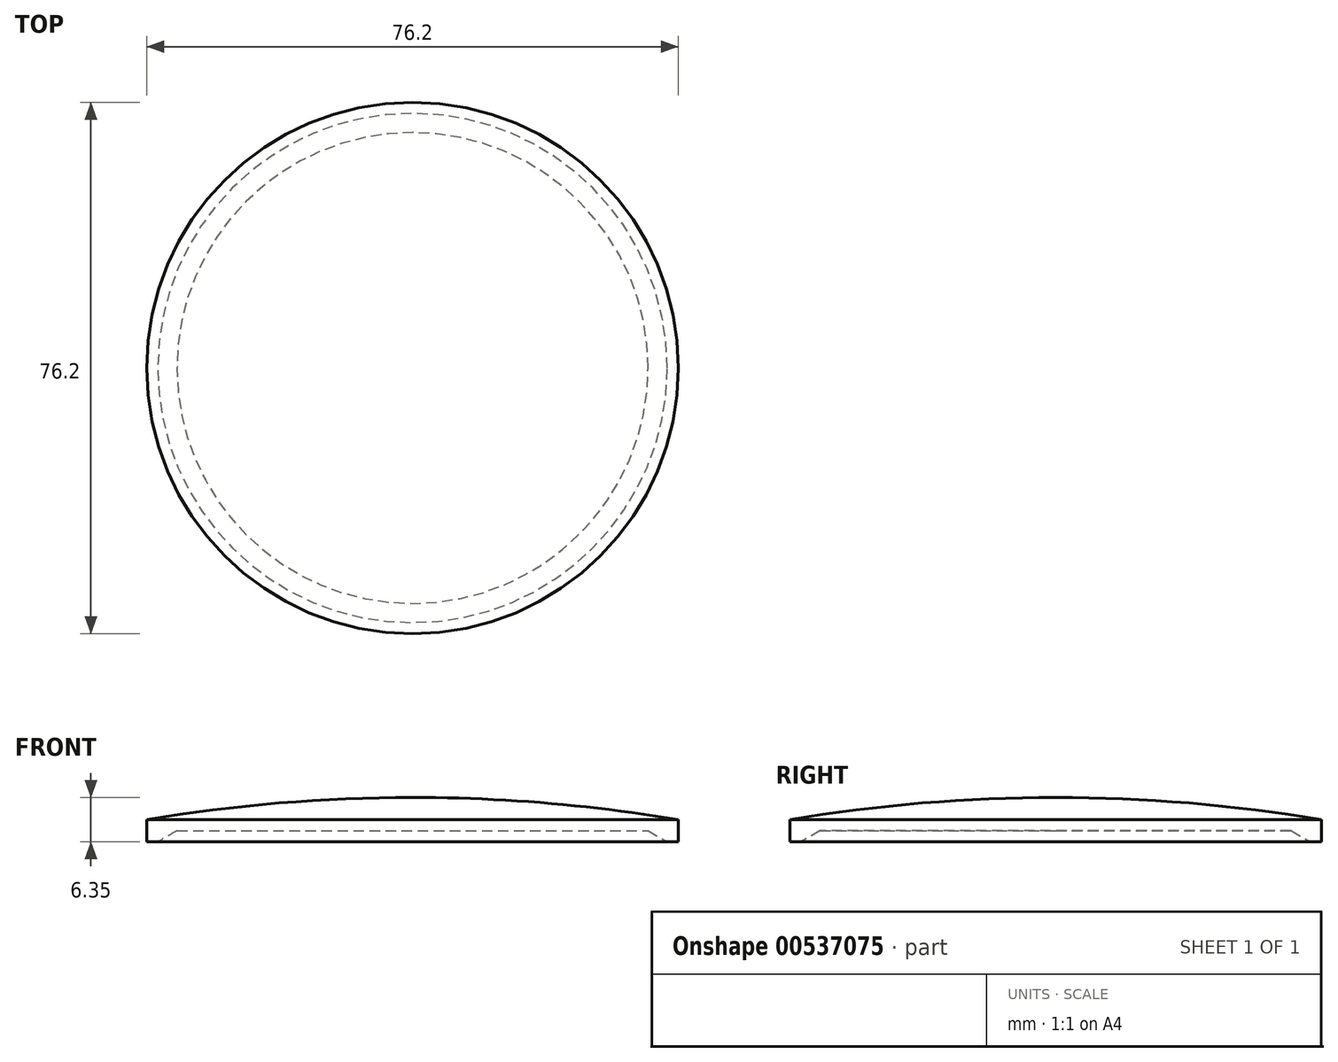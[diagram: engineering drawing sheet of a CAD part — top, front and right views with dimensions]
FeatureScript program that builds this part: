
annotation { "Feature Type Name" : "Feature", "Feature Type Description" : "" }
export const myFeature = defineFeature(function(context is Context, id is Id, definition is map)
    precondition{}
    {
        {
            var Q0;
            Q0=qCreatedBy(makeId("Front.planeOp"),FACE);
            var sketch = newSketch(context, id + "F0", { "sketchPlane" : qUnion([Q0])});
            skLineSegment(sketch, "E0", {"start": v(36.51, 0) * mm, "end": v(38.1, 0) * mm});
            skLineSegment(sketch, "E1.MirrorCS", {"start": v(33.76, 1.59) * mm, "end": v(36.51, 0) * mm});
            skLineSegment(sketch, "E2.MirrorCS", {"start": v(38.1, 0) * mm, "end": v(38.1, 3.18) * mm});
            skLineSegment(sketch, "E3.MirrorCS", {"start": v(0, 1.59) * mm, "end": v(0, 6.35) * mm});
            skLineSegment(sketch, "E4.MirrorCS", {"start": v(33.76, 1.59) * mm, "end": v(0, 1.59) * mm});
            skArc(sketch, "E5.MirrorCS", {"start": v(0, 6.35) * mm, "mid": v(19.12, 5.55) * mm, "end": v(38.1, 3.18) * mm});
            skSolve(sketch);
        }
        {
            var Q0;
            Q0=qSketchRegion(id+"F0",true);
            var Q1;
            Q1=sQuery(id+"F0.wireOp",EDGE,"E3.MirrorCS");
            revolve(context, id + "F1", {"entities" : qUnion([Q0]), "axis" : qUnion([Q1]), "revolveType" : RevolveType.FULL});
        }
    });
